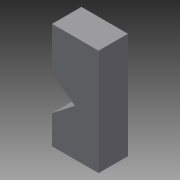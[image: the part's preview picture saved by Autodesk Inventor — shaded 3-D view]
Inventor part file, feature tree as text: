
AUTODESK INVENTOR PART (.ipt)
format: ipt  version: 2015 (Build 190159000, 159)  size: 78,848 bytes
history: native  units: mm
features: extrude x2, sketch x2, projected_geometry x1
ambient origin geometry x8: Origin, YZ Plane, XZ Plane, XY Plane, X Axis, Y Axis, Z Axis, Center Point
bodies: Solid1 (feature_tree)
feature tree (5):
  extrude  "Extrusion1"  Depth=5.0mm TaperAngle=0.0deg
  extrude  "Extrusion2"  [1 undecoded]
  sketch  "Sketch1"  dims[d0=5.0mm d1=0.0mm d2=5.0mm d3=0.0mm]
  sketch  "Sketch2"
  projected_geometry  "Projected Loop1"
note: 1 required parameter value undecoded (feature->parameter linkage not recoverable at this tier; creation-order binding heuristic only, values carry confidence <= 0.55)
